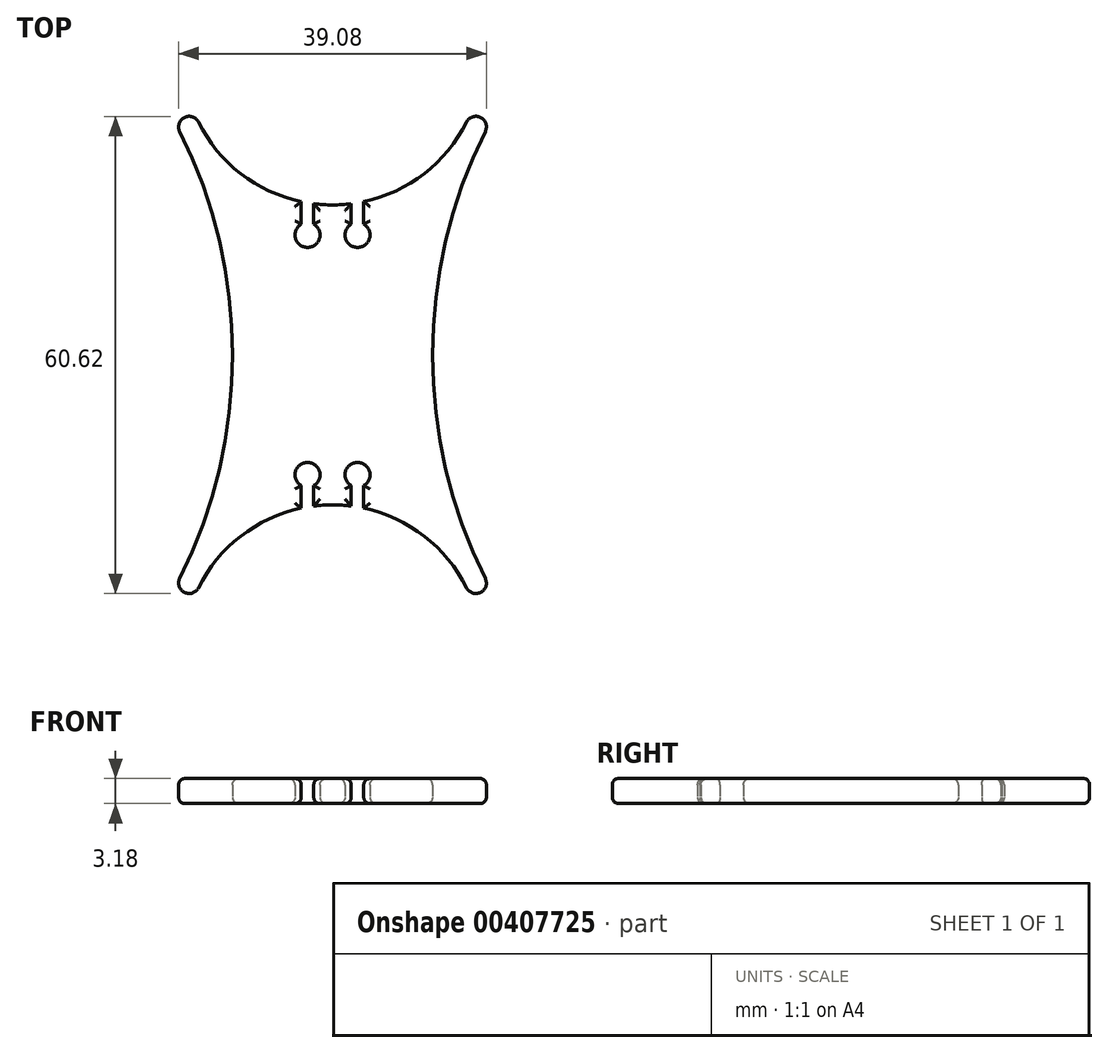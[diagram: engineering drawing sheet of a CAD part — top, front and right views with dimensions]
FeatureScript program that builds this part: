
annotation { "Feature Type Name" : "Feature", "Feature Type Description" : "" }
export const myFeature = defineFeature(function(context is Context, id is Id, definition is map)
    precondition{}
    {
        {
            var Q0;
            Q0=qCreatedBy(makeId("Top.planeOp"),FACE);
            var sketch = newSketch(context, id + "F0", { "sketchPlane" : qUnion([Q0])});
            skArc(sketch, "E0", {"start": v(-17.04, 29.58) * mm, "mid": v(-11.66, 23.03) * mm, "end": v(-3.97, 19.47) * mm});
            skArc(sketch, "E1.MirrorC", {"start": v(-17.04, -29.58) * mm, "mid": v(-11.66, -23.03) * mm, "end": v(-3.97, -19.47) * mm});
            skArc(sketch, "E2", {"start": v(19.4, 28.4) * mm, "mid": v(12.7, 0) * mm, "end": v(19.4, -28.4) * mm});
            skArc(sketch, "E3.MirrorC", {"start": v(-19.4, 28.4) * mm, "mid": v(-12.7, 0) * mm, "end": v(-19.4, -28.4) * mm});
            skLineSegment(sketch, "E4", {"start": v(17.04, 29.58) * mm, "end": v(19.4, 28.4) * mm, "construction": true});
            skArc(sketch, "E5", {"start": v(19.4, 28.4) * mm, "mid": v(18.81, 30.17) * mm, "end": v(17.04, 29.58) * mm});
            skArc(sketch, "E6.MirrorC", {"start": v(-19.4, 28.4) * mm, "mid": v(-18.81, 30.17) * mm, "end": v(-17.04, 29.58) * mm});
            skArc(sketch, "E7.MirrorC", {"start": v(-19.4, -28.4) * mm, "mid": v(-18.81, -30.17) * mm, "end": v(-17.04, -29.58) * mm});
            skArc(sketch, "E8.MirrorC", {"start": v(19.4, -28.4) * mm, "mid": v(18.81, -30.17) * mm, "end": v(17.04, -29.58) * mm});
            skArc(sketch, "E9", {"start": v(-2.38, -16.61) * mm, "mid": v(-3.18, -13.65) * mm, "end": v(-3.97, -16.61) * mm});
            skLineSegment(sketch, "E10", {"start": v(-3.17, -15.24) * mm, "end": v(-3.17, -17.36) * mm, "construction": true});
            skLineSegment(sketch, "E11.0", {"start": v(-3.97, -16.61) * mm, "end": v(-3.97, -19.47) * mm});
            skLineSegment(sketch, "E12.MirrorCS", {"start": v(-2.38, -16.61) * mm, "end": v(-2.38, -19.2) * mm});
            skPoint(sketch, "E13.orphan", {"position": v(-3.97, -10.16) * mm});
            skPoint(sketch, "E14.orphan", {"position": v(-2.38, -10.16) * mm});
            skArc(sketch, "E15.trimOffspring", {"start": v(-2.38, -19.2) * mm, "mid": v(0, -19.05) * mm, "end": v(2.38, -19.2) * mm});
            skPoint(sketch, "E16.orphan", {"position": v(-2.38, -17.36) * mm});
            skPoint(sketch, "E17.orphan", {"position": v(-3.97, -17.36) * mm});
            skLineSegment(sketch, "E18.MirrorCS", {"start": v(2.38, -16.61) * mm, "end": v(2.38, -19.2) * mm});
            skLineSegment(sketch, "E19.MirrorCS", {"start": v(3.17, -15.24) * mm, "end": v(3.17, -17.36) * mm, "construction": true});
            skLineSegment(sketch, "E20.MirrorCS", {"start": v(3.97, -16.61) * mm, "end": v(3.97, -19.47) * mm});
            skArc(sketch, "E21.MirrorCS", {"start": v(2.38, -16.61) * mm, "mid": v(3.18, -13.65) * mm, "end": v(3.97, -16.61) * mm});
            skLineSegment(sketch, "E22.MirrorCS", {"start": v(3.97, 16.61) * mm, "end": v(3.97, 19.47) * mm});
            skArc(sketch, "E23.MirrorCS", {"start": v(2.38, 16.61) * mm, "mid": v(3.18, 13.65) * mm, "end": v(3.97, 16.61) * mm});
            skLineSegment(sketch, "E24.MirrorCS", {"start": v(2.38, 16.61) * mm, "end": v(2.38, 19.2) * mm});
            skLineSegment(sketch, "E25.MirrorCS", {"start": v(-3.97, 16.61) * mm, "end": v(-3.97, 19.47) * mm});
            skLineSegment(sketch, "E26.MirrorCS", {"start": v(-2.38, 16.61) * mm, "end": v(-2.38, 19.2) * mm});
            skArc(sketch, "E27.MirrorCS", {"start": v(-2.38, 16.61) * mm, "mid": v(-3.18, 13.65) * mm, "end": v(-3.97, 16.61) * mm});
            skArc(sketch, "E28.trimOffspring", {"start": v(-2.38, 19.2) * mm, "mid": v(0, 19.05) * mm, "end": v(2.38, 19.2) * mm});
            skArc(sketch, "E29.trimOffspring", {"start": v(3.97, 19.47) * mm, "mid": v(11.66, 23.03) * mm, "end": v(17.04, 29.58) * mm});
            skArc(sketch, "E30.trimOffspring", {"start": v(3.97, -19.47) * mm, "mid": v(11.66, -23.03) * mm, "end": v(17.04, -29.58) * mm});
            skSolve(sketch);
        }
        {
            var Q0;
            Q0=makeQuery(id+"F0.imprint","IMPRINT",FACE,{"disambiguationData":[TD([[makeQuery(id+"F0.imprint","IMPRINT",EDGE,{"derivedFrom":sQuery(id+"F0.wireOp",EDGE,"E0")}),-1.0]])]});
            extrude(context, id + "F1", {"entities" : qUnion([Q0]), "depth" : 3.17 * mm});
        }
        {
            var Q0;
            Q0=makeQuery(id+"F1.opExtrude","CAP_FACE",FACE,{"disambiguationData":[OSD([sQuery(id+"F0.wireOp",EDGE,"E0"),sQuery(id+"F0.wireOp",EDGE,"E1.MirrorC"),sQuery(id+"F0.wireOp",EDGE,"E2"),sQuery(id+"F0.wireOp",EDGE,"E3.MirrorC"),sQuery(id+"F0.wireOp",EDGE,"E5"),sQuery(id+"F0.wireOp",EDGE,"E6.MirrorC"),sQuery(id+"F0.wireOp",EDGE,"E7.MirrorC"),sQuery(id+"F0.wireOp",EDGE,"E8.MirrorC"),sQuery(id+"F0.wireOp",EDGE,"E9"),sQuery(id+"F0.wireOp",EDGE,"E11.0"),sQuery(id+"F0.wireOp",EDGE,"E12.MirrorCS"),sQuery(id+"F0.wireOp",EDGE,"E15.trimOffspring"),sQuery(id+"F0.wireOp",EDGE,"E18.MirrorCS"),sQuery(id+"F0.wireOp",EDGE,"E20.MirrorCS"),sQuery(id+"F0.wireOp",EDGE,"E21.MirrorCS"),sQuery(id+"F0.wireOp",EDGE,"E22.MirrorCS"),sQuery(id+"F0.wireOp",EDGE,"E23.MirrorCS"),sQuery(id+"F0.wireOp",EDGE,"E24.MirrorCS"),sQuery(id+"F0.wireOp",EDGE,"E25.MirrorCS"),sQuery(id+"F0.wireOp",EDGE,"E26.MirrorCS"),sQuery(id+"F0.wireOp",EDGE,"E27.MirrorCS"),sQuery(id+"F0.wireOp",EDGE,"E28.trimOffspring"),sQuery(id+"F0.wireOp",EDGE,"E29.trimOffspring"),sQuery(id+"F0.wireOp",EDGE,"E30.trimOffspring")])],"isStart":false});
            var Q1;
            Q1=makeQuery(id+"F1.opExtrude","CAP_FACE",FACE,{"disambiguationData":[OSD([sQuery(id+"F0.wireOp",EDGE,"E0"),sQuery(id+"F0.wireOp",EDGE,"E1.MirrorC"),sQuery(id+"F0.wireOp",EDGE,"E2"),sQuery(id+"F0.wireOp",EDGE,"E3.MirrorC"),sQuery(id+"F0.wireOp",EDGE,"E5"),sQuery(id+"F0.wireOp",EDGE,"E6.MirrorC"),sQuery(id+"F0.wireOp",EDGE,"E7.MirrorC"),sQuery(id+"F0.wireOp",EDGE,"E8.MirrorC"),sQuery(id+"F0.wireOp",EDGE,"E9"),sQuery(id+"F0.wireOp",EDGE,"E11.0"),sQuery(id+"F0.wireOp",EDGE,"E12.MirrorCS"),sQuery(id+"F0.wireOp",EDGE,"E15.trimOffspring"),sQuery(id+"F0.wireOp",EDGE,"E18.MirrorCS"),sQuery(id+"F0.wireOp",EDGE,"E20.MirrorCS"),sQuery(id+"F0.wireOp",EDGE,"E21.MirrorCS"),sQuery(id+"F0.wireOp",EDGE,"E22.MirrorCS"),sQuery(id+"F0.wireOp",EDGE,"E23.MirrorCS"),sQuery(id+"F0.wireOp",EDGE,"E24.MirrorCS"),sQuery(id+"F0.wireOp",EDGE,"E25.MirrorCS"),sQuery(id+"F0.wireOp",EDGE,"E26.MirrorCS"),sQuery(id+"F0.wireOp",EDGE,"E27.MirrorCS"),sQuery(id+"F0.wireOp",EDGE,"E28.trimOffspring"),sQuery(id+"F0.wireOp",EDGE,"E29.trimOffspring"),sQuery(id+"F0.wireOp",EDGE,"E30.trimOffspring")])],"isStart":true});
            fillet(context, id + "F2", {"entities" : qUnion([Q0, Q1]), "radius" : 0.8 * mm, "tangentPropagation" : true, "allowEdgeOverflow" : false});
        }
    });
